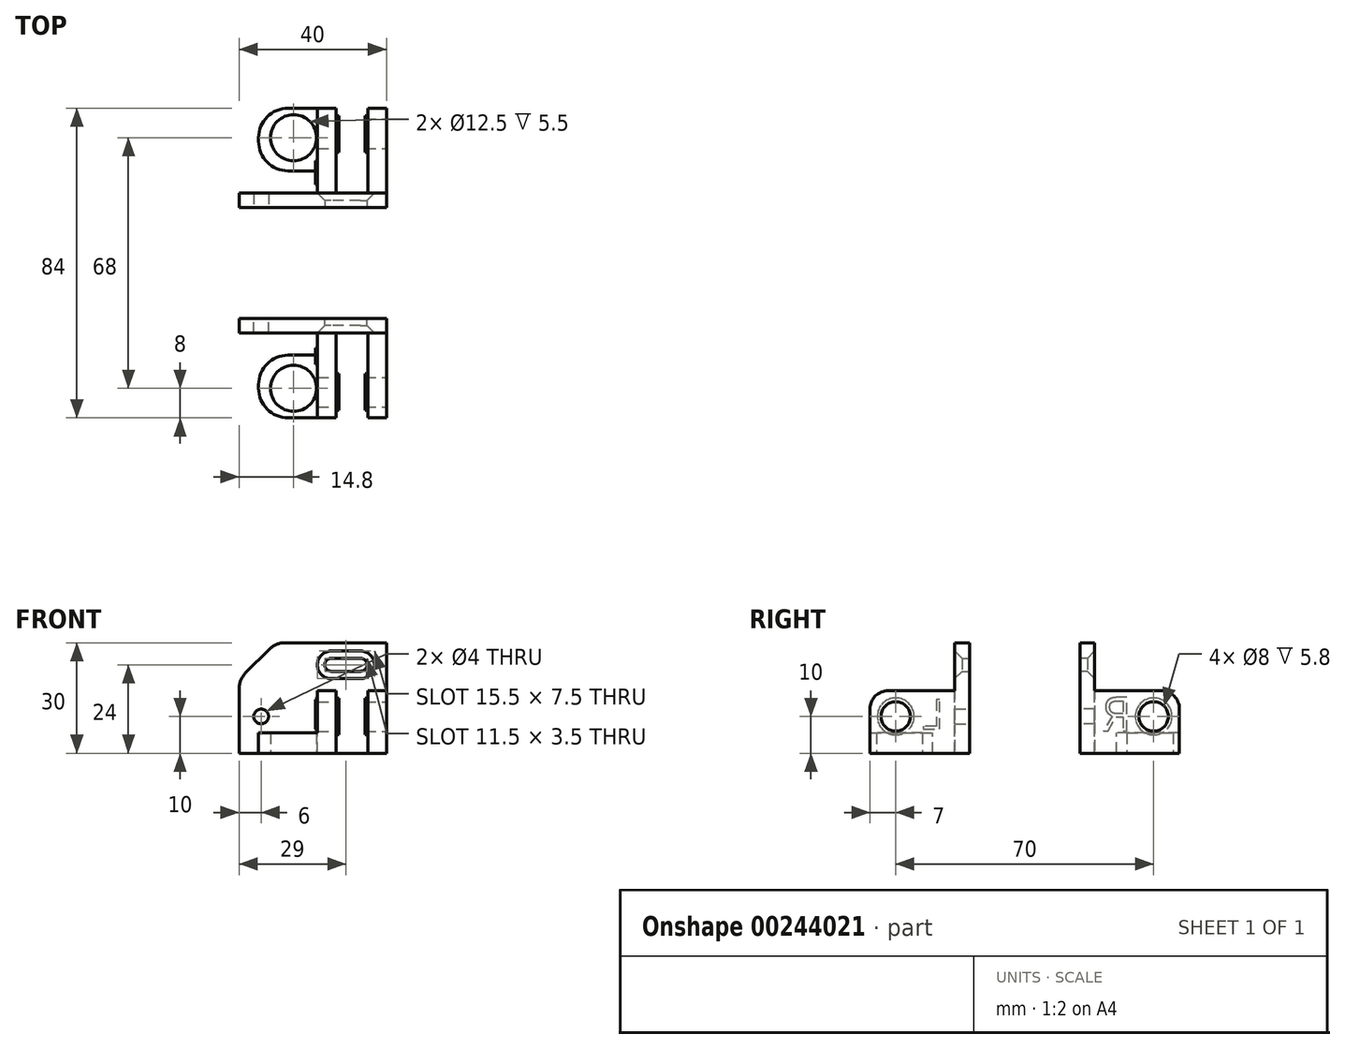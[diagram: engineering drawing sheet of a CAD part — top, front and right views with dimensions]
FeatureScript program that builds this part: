
annotation { "Feature Type Name" : "Feature", "Feature Type Description" : "" }
export const myFeature = defineFeature(function(context is Context, id is Id, definition is map)
    precondition{}
    {
        {
            var Q0;
            Q0=qCreatedBy(makeId("Top.planeOp"),FACE);
            var sketch = newSketch(context, id + "F0", { "sketchPlane" : qUnion([Q0])});
            skLineSegment(sketch, "E0.rect.bottom", {"start": v(-20, 15) * mm, "end": v(20, 15) * mm});
            skLineSegment(sketch, "E0.rect.top", {"start": v(-20, -15) * mm, "end": v(20, -15) * mm});
            skLineSegment(sketch, "E0.rect.left", {"start": v(-20, 15) * mm, "end": v(-20, -15) * mm});
            skLineSegment(sketch, "E0.rect.right", {"start": v(20, 15) * mm, "end": v(20, -15) * mm});
            skPoint(sketch, "E0.rect.middle", {"position": v(0, 0) * mm});
            skLineSegment(sketch, "E1", {"start": v(22.5, 9) * mm, "end": v(-29.72, 9) * mm, "construction": true});
            skLineSegment(sketch, "E2", {"start": v(13, 13.7) * mm, "end": v(13, 4.14) * mm, "construction": true});
            skLineSegment(sketch, "E3", {"start": v(5, 13.23) * mm, "end": v(5, 3.86) * mm, "construction": true});
            skLineSegment(sketch, "E4.bottom", {"start": v(5, 10.75) * mm, "end": v(13, 10.75) * mm});
            skLineSegment(sketch, "E4.top", {"start": v(5, 7.25) * mm, "end": v(13, 7.25) * mm});
            skLineSegment(sketch, "E4.left", {"start": v(5, 10.75) * mm, "end": v(5, 7.25) * mm});
            skLineSegment(sketch, "E4.right", {"start": v(13, 10.75) * mm, "end": v(13, 7.25) * mm});
            skCircle(sketch, "E5", {"center": v(5, 9) * mm, "radius": 1.75 * mm});
            skCircle(sketch, "E6", {"center": v(13, 9) * mm, "radius": 1.75 * mm});
            skLineSegment(sketch, "E7", {"start": v(-14, 2.4) * mm, "end": v(-14, -11.6) * mm, "construction": true});
            skLineSegment(sketch, "E8", {"start": v(-21.97, -5) * mm, "end": v(-8.17, -5) * mm, "construction": true});
            skCircle(sketch, "E9", {"center": v(-14, -5) * mm, "radius": 2 * mm});
            skSolve(sketch);
        }
        {
            var Q0;
            Q0=qSketchRegion(id+"F0",true);
            extrude(context, id + "F1", {"entities" : qUnion([Q0]), "depth" : 4 * mm});
        }
        {
            var Q0;
            Q0=makeQuery(id+"F1.opExtrude","CAP_EDGE",EDGE,{"disambiguationData":[OSD([sQuery(id+"F0.wireOp",EDGE,"E4.bottom")])],"isStart":false});
            chamfer(context, id + "F2", {"entities" : qUnion([Q0]), "width" : 2 * mm, "tangentPropagation" : true});
        }
        {
            var Q0;
            Q0=makeQuery(id+"F1.opExtrude","SWEPT_EDGE",EDGE,{"disambiguationData":[OSD([sQuery(id+"F0.wireOp",EDGE,"E0.rect.bottom"),sQuery(id+"F0.wireOp",EDGE,"E0.rect.left")])]});
            chamfer(context, id + "F3", {"entities" : qUnion([Q0]), "width" : 10 * mm, "tangentPropagation" : true});
        }
        {
            var Q0;
            {var subQ0=sQuery(id+"F0.wireOp",EDGE,"E0.rect.bottom");Q0=makeQuery(id+"F3.opChamfer","BLEND_EDGE",EDGE,{"blendedFrom":[makeQuery(id+"F1.opExtrude","SWEPT_EDGE",EDGE,{"disambiguationData":[OSD([subQ0,sQuery(id+"F0.wireOp",EDGE,"E0.rect.left")])]}),makeQuery(id+"F1.opExtrude","SWEPT_FACE",FACE,{"disambiguationData":[OSD([subQ0])]})],"blendedInto":[makeQuery(id+"F1.opExtrude","SWEPT_FACE",FACE,{"disambiguationData":[OSD([subQ0])]})]});}
            var Q1;
            {var subQ0=sQuery(id+"F0.wireOp",EDGE,"E0.rect.left");Q1=makeQuery(id+"F3.opChamfer","BLEND_EDGE",EDGE,{"blendedFrom":[makeQuery(id+"F1.opExtrude","SWEPT_EDGE",EDGE,{"disambiguationData":[OSD([sQuery(id+"F0.wireOp",EDGE,"E0.rect.bottom"),subQ0])]}),makeQuery(id+"F1.opExtrude","SWEPT_FACE",FACE,{"disambiguationData":[OSD([subQ0])]})],"blendedInto":[makeQuery(id+"F1.opExtrude","SWEPT_FACE",FACE,{"disambiguationData":[OSD([subQ0])]})]});}
            fillet(context, id + "F4", {"entities" : qUnion([Q0, Q1]), "radius" : 6 * mm, "tangentPropagation" : true, "allowEdgeOverflow" : false});
        }
        {
            var Q0;
            Q0=makeQuery(id+"F1.opExtrude","CAP_FACE",FACE,{"disambiguationData":[OSD([sQuery(id+"F0.wireOp",EDGE,"E0.rect.bottom"),sQuery(id+"F0.wireOp",EDGE,"E0.rect.top"),sQuery(id+"F0.wireOp",EDGE,"E0.rect.left"),sQuery(id+"F0.wireOp",EDGE,"E0.rect.right"),sQuery(id+"F0.wireOp",EDGE,"E4.bottom"),sQuery(id+"F0.wireOp",EDGE,"E4.top"),sQuery(id+"F0.wireOp",EDGE,"E5"),sQuery(id+"F0.wireOp",EDGE,"E6")])],"isStart":false});
            var sketch = newSketch(context, id + "F5", { "sketchPlane" : qUnion([Q0])});
            skLineSegment(sketch, "E10.bottom", {"start": v(20, -15) * mm, "end": v(15, -15) * mm});
            skLineSegment(sketch, "E10.top", {"start": v(20, 2) * mm, "end": v(15, 2) * mm});
            skLineSegment(sketch, "E10.left", {"start": v(20, -15) * mm, "end": v(20, 2) * mm});
            skLineSegment(sketch, "E10.right", {"start": v(15, -15) * mm, "end": v(15, 2) * mm});
            skLineSegment(sketch, "E11.bottom", {"start": v(6.3, -15) * mm, "end": v(1.3, -15) * mm});
            skLineSegment(sketch, "E11.top", {"start": v(6.3, 2) * mm, "end": v(1.3, 2) * mm});
            skLineSegment(sketch, "E11.left", {"start": v(6.3, -15) * mm, "end": v(6.3, 2) * mm});
            skLineSegment(sketch, "E11.right", {"start": v(1.3, -15) * mm, "end": v(1.3, 2) * mm});
            skSolve(sketch);
        }
        {
            var Q0;
            Q0=qSketchRegion(id+"F5",true);
            extrude(context, id + "F6", {"entities" : qUnion([Q0]), "operationType" : NewBodyOperationType.ADD, "depth" : 23 * mm});
        }
        {
            var Q0;
            Q0=makeQuery(id+"F6.opExtrude","CAP_EDGE",EDGE,{"disambiguationData":[OSD([sQuery(id+"F5.wireOp",EDGE,"E10.top")])],"isStart":false});
            var Q1;
            Q1=makeQuery(id+"F6.opExtrude","CAP_EDGE",EDGE,{"disambiguationData":[OSD([sQuery(id+"F5.wireOp",EDGE,"E11.top")])],"isStart":false});
            var Q2;
            Q2=makeQuery(id+"F6.opExtrude","CAP_EDGE",EDGE,{"disambiguationData":[OSD([sQuery(id+"F5.wireOp",EDGE,"E11.top")])],"isStart":true});
            var Q3;
            Q3=makeQuery(id+"F6.opExtrude","CAP_EDGE",EDGE,{"disambiguationData":[OSD([sQuery(id+"F5.wireOp",EDGE,"E10.top")])],"isStart":true});
            fillet(context, id + "F7", {"entities" : qUnion([Q0, Q1, Q2, Q3]), "radius" : 5 * mm, "tangentPropagation" : true, "allowEdgeOverflow" : false});
        }
        {
            var Q0;
            Q0=makeQuery(id+"F6.boolean.opBoolean","MERGE",FACE,{"derivedFrom":[makeQuery(id+"F1.opExtrude","SWEPT_FACE",FACE,{"disambiguationData":[OSD([sQuery(id+"F0.wireOp",EDGE,"E0.rect.right")])]}),makeQuery(id+"F6.opExtrude","SWEPT_FACE",FACE,{"disambiguationData":[OSD([sQuery(id+"F5.wireOp",EDGE,"E10.left")])]})]});
            var sketch = newSketch(context, id + "F8", { "sketchPlane" : qUnion([Q0])});
            skLineSegment(sketch, "E12", {"start": v(-5, 33.9) * mm, "end": v(-5, -7.2) * mm, "construction": true});
            skLineSegment(sketch, "E13", {"start": v(-23.25, 20) * mm, "end": v(17.75, 20) * mm, "construction": true});
            skCircle(sketch, "E14", {"center": v(-5, 20) * mm, "radius": 4 * mm});
            skSolve(sketch);
        }
        {
            var Q0;
            Q0=sQuery(id+"F8.wireOp",VERTEX,"E14.center");
            var Q1;
            Q1=makeQuery(id+"F1.opExtrude","SWEPT_BODY",BODY,{"disambiguationData":[OSD([sQuery(id+"F0.wireOp",EDGE,"E0.rect.bottom"),sQuery(id+"F0.wireOp",EDGE,"E0.rect.top"),sQuery(id+"F0.wireOp",EDGE,"E0.rect.left"),sQuery(id+"F0.wireOp",EDGE,"E0.rect.right"),sQuery(id+"F0.wireOp",EDGE,"E4.bottom"),sQuery(id+"F0.wireOp",EDGE,"E4.top"),sQuery(id+"F0.wireOp",EDGE,"E5"),sQuery(id+"F0.wireOp",EDGE,"E6")])]});
            hole(context, id + "F9", {"style" : HoleStyle.SIMPLE, "holeDiameter" : 8 * mm, "endStyle" : HoleEndStyle.THROUGH, "locations" : qUnion([Q0]), "scope" : qUnion([Q1])});
        }
        {
            var Q0;
            Q0=makeQuery(id+"F6.opExtrude","SWEPT_FACE",FACE,{"disambiguationData":[OSD([sQuery(id+"F5.wireOp",EDGE,"E11.right")])]});
            var sketch = newSketch(context, id + "F10", { "sketchPlane" : qUnion([Q0])});
            skLineSegment(sketch, "E15.bottom", {"start": v(15, 27) * mm, "end": v(9.5, 27) * mm});
            skLineSegment(sketch, "E15.top", {"start": v(15, 10) * mm, "end": v(9.5, 10) * mm});
            skLineSegment(sketch, "E15.left", {"start": v(15, 27) * mm, "end": v(15, 10) * mm});
            skLineSegment(sketch, "E15.right", {"start": v(9.5, 27) * mm, "end": v(9.5, 10) * mm});
            skSolve(sketch);
        }
        {
            var Q0;
            Q0=qSketchRegion(id+"F10",true);
            extrude(context, id + "F11", {"entities" : qUnion([Q0]), "operationType" : NewBodyOperationType.ADD, "depth" : 16 * mm});
        }
        {
            var Q0;
            Q0=makeQuery(id+"F11.opExtrude","CAP_EDGE",EDGE,{"disambiguationData":[OSD([sQuery(id+"F10.wireOp",EDGE,"E15.bottom")])],"isStart":false});
            var Q1;
            Q1=makeQuery(id+"F11.opExtrude","CAP_EDGE",EDGE,{"disambiguationData":[OSD([sQuery(id+"F10.wireOp",EDGE,"E15.top")])],"isStart":false});
            fillet(context, id + "F12", {"entities" : qUnion([Q0, Q1]), "radius" : 8 * mm, "tangentPropagation" : true, "allowEdgeOverflow" : false});
        }
        {
            var Q0;
            Q0=makeQuery(id+"F11.boolean.opBoolean","MERGE",FACE,{"derivedFrom":[makeQuery(id+"F6.boolean.opBoolean","MERGE",FACE,{"derivedFrom":[makeQuery(id+"F1.opExtrude","SWEPT_FACE",FACE,{"disambiguationData":[OSD([sQuery(id+"F0.wireOp",EDGE,"E0.rect.top")])]}),makeQuery(id+"F6.opExtrude","SWEPT_FACE",FACE,{"disambiguationData":[OSD([sQuery(id+"F5.wireOp",EDGE,"E10.bottom")])]}),makeQuery(id+"F6.opExtrude","SWEPT_FACE",FACE,{"disambiguationData":[OSD([sQuery(id+"F5.wireOp",EDGE,"E11.bottom")])]})]}),makeQuery(id+"F11.opExtrude","SWEPT_FACE",FACE,{"disambiguationData":[OSD([sQuery(id+"F10.wireOp",EDGE,"E15.left")])]})]});
            var sketch = newSketch(context, id + "F13", { "sketchPlane" : qUnion([Q0])});
            skPoint(sketch, "E16", {"position": v(-5.2, 19) * mm});
            skSolve(sketch);
        }
        {
            var Q0;
            Q0=sQuery(id+"F13.wireOp",VERTEX,"E16");
            var Q1;
            Q1=makeQuery(id+"F1.opExtrude","SWEPT_BODY",BODY,{"disambiguationData":[OSD([sQuery(id+"F0.wireOp",EDGE,"E0.rect.bottom"),sQuery(id+"F0.wireOp",EDGE,"E0.rect.top"),sQuery(id+"F0.wireOp",EDGE,"E0.rect.left"),sQuery(id+"F0.wireOp",EDGE,"E0.rect.right"),sQuery(id+"F0.wireOp",EDGE,"E4.bottom"),sQuery(id+"F0.wireOp",EDGE,"E4.top"),sQuery(id+"F0.wireOp",EDGE,"E5"),sQuery(id+"F0.wireOp",EDGE,"E6")])]});
            hole(context, id + "F14", {"style" : HoleStyle.SIMPLE, "holeDiameter" : 12.5 * mm, "endStyle" : HoleEndStyle.THROUGH, "locations" : qUnion([Q0]), "scope" : qUnion([Q1]), "tappedDepth" : 12 * mm, "tapClearance" : 3});
        }
        {
            var Q0;
            Q0=makeQuery(id+"F1.opExtrude","SWEPT_BODY",BODY,{"disambiguationData":[OSD([sQuery(id+"F0.wireOp",EDGE,"E0.rect.bottom"),sQuery(id+"F0.wireOp",EDGE,"E0.rect.top"),sQuery(id+"F0.wireOp",EDGE,"E0.rect.left"),sQuery(id+"F0.wireOp",EDGE,"E0.rect.right"),sQuery(id+"F0.wireOp",EDGE,"E4.bottom"),sQuery(id+"F0.wireOp",EDGE,"E4.top"),sQuery(id+"F0.wireOp",EDGE,"E5"),sQuery(id+"F0.wireOp",EDGE,"E6"),sQuery(id+"F0.wireOp",EDGE,"E9")])]});
            var Q1;
            Q1=makeQuery(id+"F1.opExtrude","CAP_EDGE",EDGE,{"disambiguationData":[OSD([sQuery(id+"F0.wireOp",EDGE,"E0.rect.top")])],"isStart":true});
            transform(context, id + "F15", {"entities" : qUnion([Q0]), "transformType" : TransformType.ROTATION, "transformAxis" : qUnion([Q1]), "angle" : 90 * degree, "makeCopy" : false});
        }
        {
            var Q0;
            Q0=makeQuery(id+"F6.opExtrude","SWEPT_FACE",FACE,{"disambiguationData":[OSD([sQuery(id+"F5.wireOp",EDGE,"E10.right")])]});
            var sketch = newSketch(context, id + "F16", { "sketchPlane" : qUnion([Q0])});
            skCircle(sketch, "E17", {"center": v(35, 10) * mm, "radius": 5 * mm});
            skSolve(sketch);
        }
        {
            var Q0;
            Q0=makeQuery(id+"F16.imprint","IMPRINT",FACE,{"disambiguationData":[TD([[makeQuery(id+"F16.imprint","IMPRINT",EDGE,{"derivedFrom":sQuery(id+"F16.wireOp",EDGE,"E17")}),1.0]])]});
            extrude(context, id + "F17", {"entities" : qUnion([Q0]), "operationType" : NewBodyOperationType.ADD, "depth" : 0.8 * mm});
        }
        {
            var Q0;
            Q0=makeQuery(id+"F6.opExtrude","SWEPT_FACE",FACE,{"disambiguationData":[OSD([sQuery(id+"F5.wireOp",EDGE,"E11.left")])]});
            var sketch = newSketch(context, id + "F18", { "sketchPlane" : qUnion([Q0])});
            skCircle(sketch, "E18", {"center": v(-35, 10) * mm, "radius": 5 * mm});
            skSolve(sketch);
        }
        {
            var Q0;
            Q0=makeQuery(id+"F18.imprint","IMPRINT",FACE,{"disambiguationData":[TD([[makeQuery(id+"F18.imprint","IMPRINT",EDGE,{"derivedFrom":sQuery(id+"F18.wireOp",EDGE,"E18")}),1.0]])]});
            extrude(context, id + "F19", {"entities" : qUnion([Q0]), "operationType" : NewBodyOperationType.ADD, "depth" : 0.8 * mm});
        }
        {
            var Q0;
            Q0=makeQuery(id+"F1.opExtrude","SWEPT_BODY",BODY,{"disambiguationData":[OSD([sQuery(id+"F0.wireOp",EDGE,"E0.rect.bottom"),sQuery(id+"F0.wireOp",EDGE,"E0.rect.top"),sQuery(id+"F0.wireOp",EDGE,"E0.rect.left"),sQuery(id+"F0.wireOp",EDGE,"E0.rect.right"),sQuery(id+"F0.wireOp",EDGE,"E4.bottom"),sQuery(id+"F0.wireOp",EDGE,"E4.top"),sQuery(id+"F0.wireOp",EDGE,"E5"),sQuery(id+"F0.wireOp",EDGE,"E6"),sQuery(id+"F0.wireOp",EDGE,"E9")])]});
            var Q1;
            Q1=qCreatedBy(makeId("Front.planeOp"),FACE);
            mirror(context, id + "F20", {"entities" : qUnion([Q0]), "mirrorPlane" : qUnion([Q1])});
        }
        {
            var Q0;
            Q0=makeQuery(id+"F6.opExtrude","SWEPT_FACE",FACE,{"disambiguationData":[OSD([sQuery(id+"F5.wireOp",EDGE,"E11.right")])]});
            var sketch = newSketch(context, id + "F21", { "sketchPlane" : qUnion([Q0])});
            skText(sketch, "E19", { "text": "L", "fontName": "OpenSans-Regular.ttf"});
            const initialGuessF21  = {"E19": [0.02194, 0.00652, 1, 0, 0.00807]};
            skSetInitialGuess(sketch, initialGuessF21);
            skSolve(sketch);
        }
        {
            var Q0;
            Q0=qSketchRegion(id+"F21",true);
            extrude(context, id + "F22", {"entities" : qUnion([Q0]), "operationType" : NewBodyOperationType.ADD, "depth" : 0.5 * mm});
        }
        {
            var Q0;
            Q0=makeQuery(id+"F20.opPattern","COPY",FACE,{"derivedFrom":makeQuery(id+"F6.opExtrude","SWEPT_FACE",FACE,{"disambiguationData":[OSD([sQuery(id+"F5.wireOp",EDGE,"E11.right")])]}),"instanceName":"1"});
            var sketch = newSketch(context, id + "F23", { "sketchPlane" : qUnion([Q0])});
            skText(sketch, "E20", { "text": "R", "fontName": "OpenSans-Regular.ttf"});
            const initialGuessF23  = {"E20": [-0.02902, 0.00603, 1, 0, 0.00921]};
            skSetInitialGuess(sketch, initialGuessF23);
            skSolve(sketch);
        }
        {
            var Q0;
            Q0=qSketchRegion(id+"F23",true);
            extrude(context, id + "F24", {"entities" : qUnion([Q0]), "operationType" : NewBodyOperationType.ADD, "depth" : 0.5 * mm});
        }
    });
